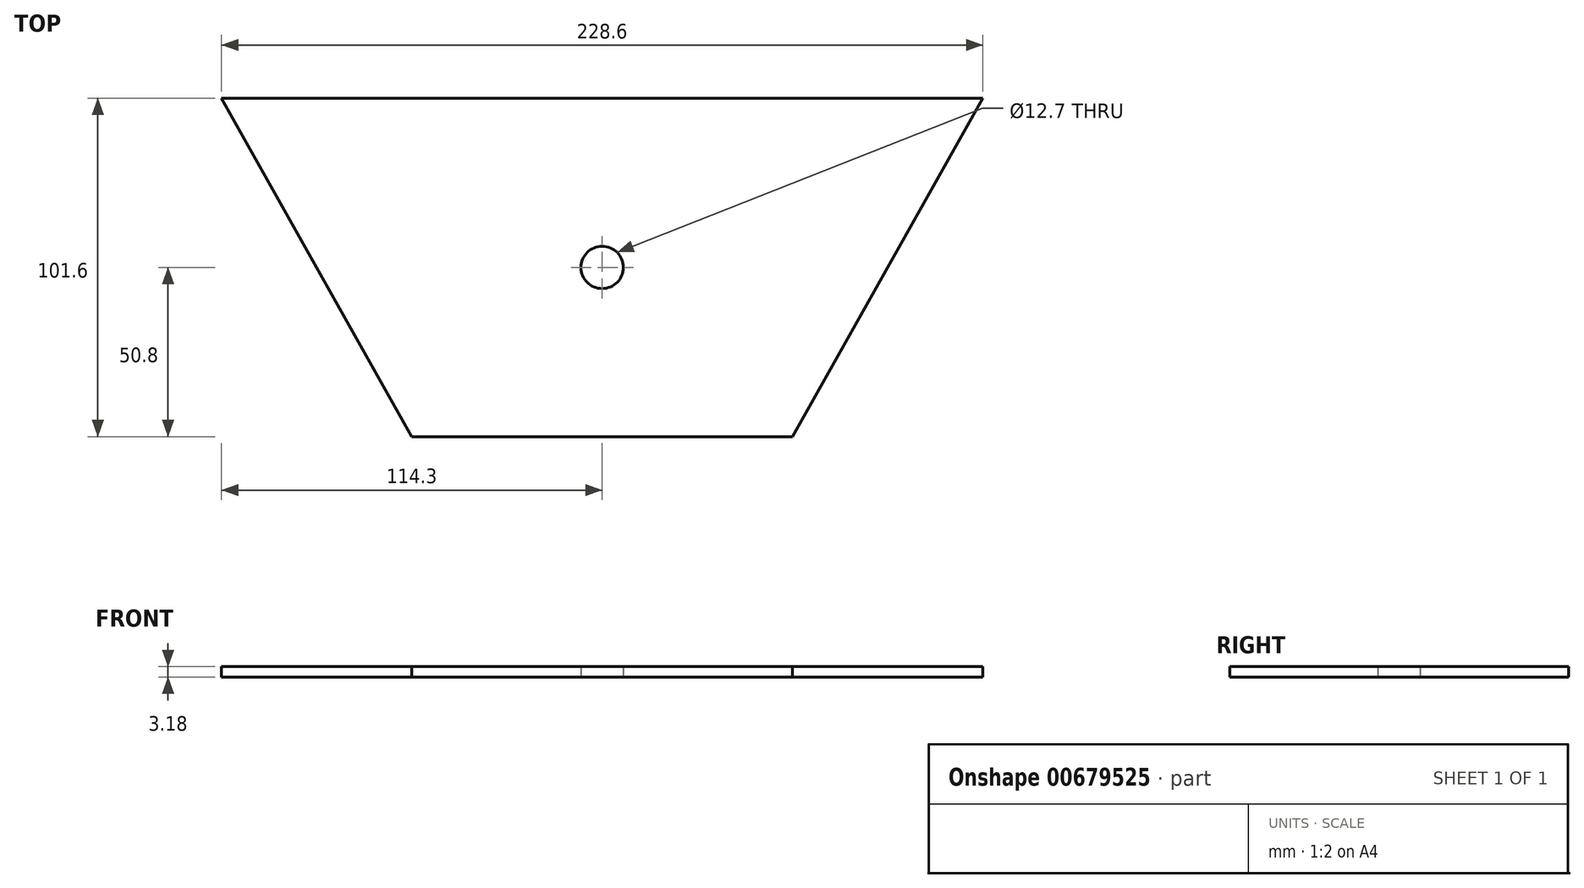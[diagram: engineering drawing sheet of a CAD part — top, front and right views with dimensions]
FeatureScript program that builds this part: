
annotation { "Feature Type Name" : "Feature", "Feature Type Description" : "" }
export const myFeature = defineFeature(function(context is Context, id is Id, definition is map)
    precondition{}
    {
        {
            var Q0;
            Q0=qCreatedBy(makeId("Top.planeOp"),FACE);
            var sketch = newSketch(context, id + "F0", { "sketchPlane" : qUnion([Q0])});
            skLineSegment(sketch, "E0.bottom", {"start": v(114.3, 50.8) * mm, "end": v(-114.3, 50.8) * mm});
            skLineSegment(sketch, "E0.top", {"start": v(57.15, -50.8) * mm, "end": v(-57.15, -50.8) * mm});
            skPoint(sketch, "E0.middle", {"position": v(0, 0) * mm});
            skLineSegment(sketch, "E1", {"start": v(-114.3, 50.8) * mm, "end": v(-57.15, -50.8) * mm});
            skLineSegment(sketch, "E2", {"start": v(-57.15, -50.8) * mm, "end": v(57.15, -50.8) * mm});
            skLineSegment(sketch, "E3", {"start": v(57.15, -50.8) * mm, "end": v(114.3, 50.8) * mm});
            skPoint(sketch, "E4.orphan", {"position": v(-114.3, -50.8) * mm});
            skPoint(sketch, "E5.orphan", {"position": v(114.3, -50.8) * mm});
            skCircle(sketch, "E6", {"center": v(0, 0) * mm, "radius": 6.35 * mm});
            skSolve(sketch);
        }
        {
            var Q0;
            Q0 = qSketchRegion(id + "F0", true);
            extrude(context, id + "F1", {"entities" : qUnion([Q0]), "depth" : 3.17 * mm, "offsetDistance" : 25.4 * mm});
        }
    });
